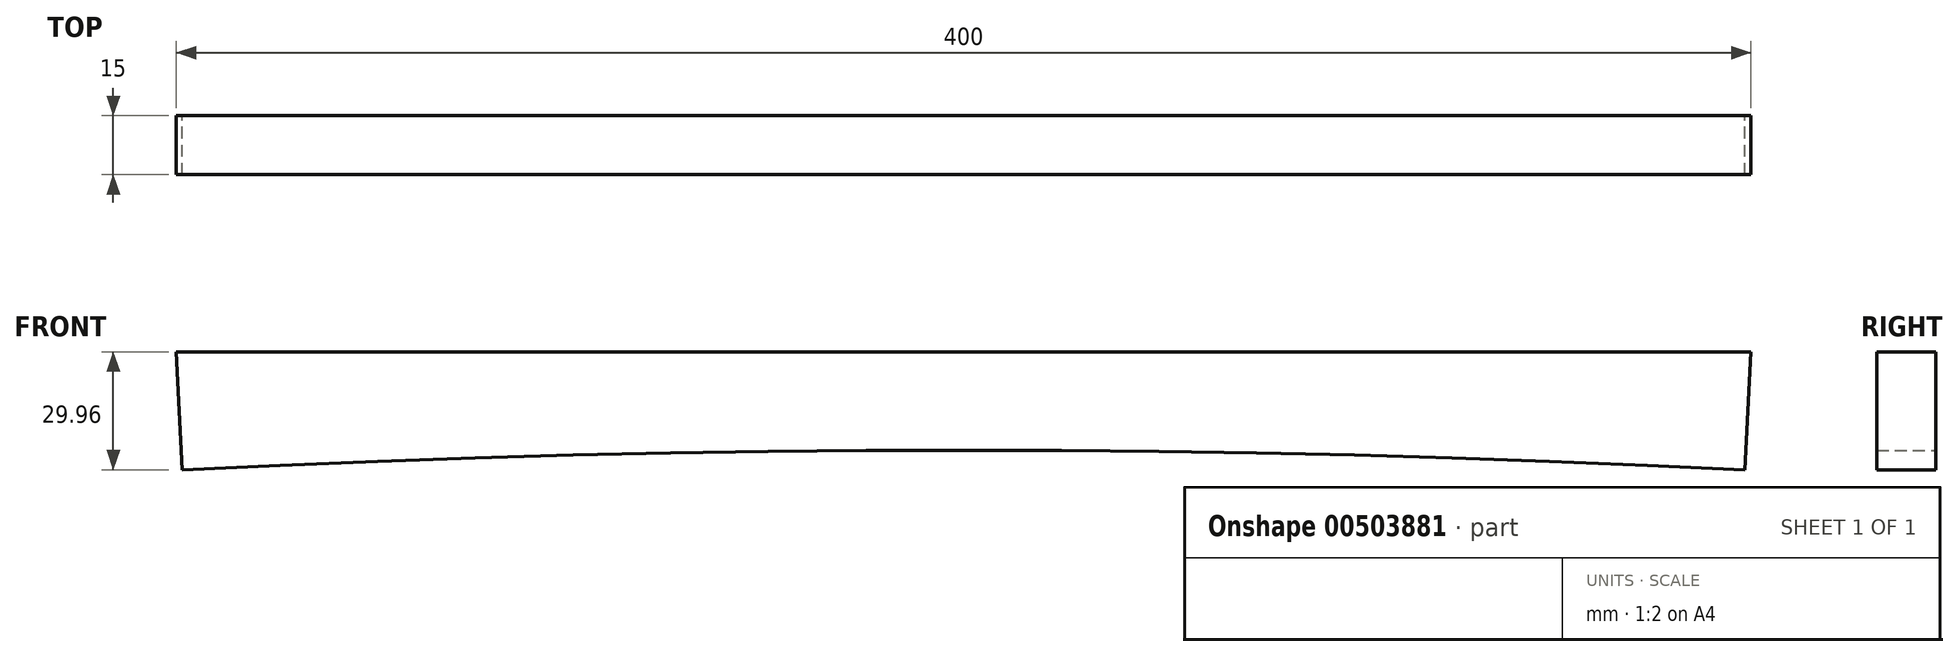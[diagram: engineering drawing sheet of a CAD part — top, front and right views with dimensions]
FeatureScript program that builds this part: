
annotation { "Feature Type Name" : "Feature", "Feature Type Description" : "" }
export const myFeature = defineFeature(function(context is Context, id is Id, definition is map)
    precondition{}
    {
        {
            var Q0;
            Q0=qCreatedBy(makeId("Front.planeOp"),FACE);
            var sketch = newSketch(context, id + "F0", { "sketchPlane" : qUnion([Q0])});
            skLineSegment(sketch, "E0", {"start": v(-200, 0) * mm, "end": v(200, 0) * mm});
            skPoint(sketch, "E1", {"position": v(0, 0) * mm});
            skLineSegment(sketch, "E2", {"start": v(0, 0) * mm, "end": v(0, -4000) * mm});
            skLineSegment(sketch, "E3", {"start": v(-198.5, -29.96) * mm, "end": v(-200, 0) * mm});
            skLineSegment(sketch, "E4", {"start": v(198.5, -29.96) * mm, "end": v(200, 0) * mm});
            skPoint(sketch, "E5", {"position": v(-198.5, -29.96) * mm});
            skPoint(sketch, "E6", {"position": v(198.5, -29.96) * mm});
            skArc(sketch, "E7", {"start": v(-198.5, -29.96) * mm, "mid": v(0, -25) * mm, "end": v(198.5, -29.96) * mm});
            skPoint(sketch, "E8", {"position": v(-198.6, -27.97) * mm});
            skArc(sketch, "E9", {"start": v(-198.6, -27.97) * mm, "mid": v(0, -23) * mm, "end": v(198.6, -27.97) * mm});
            skLineSegment(sketch, "E10", {"start": v(-199.9, -2) * mm, "end": v(199.9, -2) * mm});
            skSolve(sketch);
        }
        {
            var Q0;
            {var subQ0=sQuery(id+"F0.wireOp",EDGE,"E3");var subQ1=sQuery(id+"F0.wireOp",EDGE,"E0");var subQ2=makeQuery(id+"F0.imprint","INTERSECT",VERTEX,{"derivedFrom":[subQ1,subQ0]});Q0=makeQuery(id+"F0.imprint","IMPRINT",FACE,{"disambiguationData":[TD([[makeQuery(id+"F0.imprint","IMPRINT",EDGE,{"disambiguationData":[TD([[subQ2,-1.0]])],"derivedFrom":subQ1}),-1.0]])]});}
            var Q1;
            {var subQ0=sQuery(id+"F0.wireOp",EDGE,"E7");var subQ1=sQuery(id+"F0.wireOp",EDGE,"E2");var subQ2=makeQuery(id+"F0.imprint","INTERSECT",VERTEX,{"derivedFrom":[subQ1,subQ0]});Q1=makeQuery(id+"F0.imprint","IMPRINT",FACE,{"disambiguationData":[TD([[makeQuery(id+"F0.imprint","IMPRINT",EDGE,{"disambiguationData":[TD([[subQ2,1.0]])],"derivedFrom":subQ1}),1.0]])]});}
            var Q2;
            {var subQ0=sQuery(id+"F0.wireOp",EDGE,"E10");var subQ1=sQuery(id+"F0.wireOp",EDGE,"E2");var subQ2=makeQuery(id+"F0.imprint","INTERSECT",VERTEX,{"derivedFrom":[subQ1,subQ0]});Q2=makeQuery(id+"F0.imprint","IMPRINT",FACE,{"disambiguationData":[TD([[makeQuery(id+"F0.imprint","IMPRINT",EDGE,{"disambiguationData":[TD([[subQ2,-1.0]])],"derivedFrom":subQ1}),1.0]])]});}
            var Q3;
            {var subQ0=sQuery(id+"F0.wireOp",EDGE,"E10");var subQ1=sQuery(id+"F0.wireOp",EDGE,"E2");var subQ2=makeQuery(id+"F0.imprint","INTERSECT",VERTEX,{"derivedFrom":[subQ1,subQ0]});Q3=makeQuery(id+"F0.imprint","IMPRINT",FACE,{"disambiguationData":[TD([[makeQuery(id+"F0.imprint","IMPRINT",EDGE,{"disambiguationData":[TD([[subQ2,-1.0]])],"derivedFrom":subQ1}),-1.0]])]});}
            var Q4;
            {var subQ0=sQuery(id+"F0.wireOp",EDGE,"E4");var subQ1=sQuery(id+"F0.wireOp",EDGE,"E0");var subQ2=makeQuery(id+"F0.imprint","INTERSECT",VERTEX,{"derivedFrom":[subQ1,subQ0]});Q4=makeQuery(id+"F0.imprint","IMPRINT",FACE,{"disambiguationData":[TD([[makeQuery(id+"F0.imprint","IMPRINT",EDGE,{"disambiguationData":[TD([[subQ2,1.0]])],"derivedFrom":subQ1}),-1.0]])]});}
            var Q5;
            {var subQ0=sQuery(id+"F0.wireOp",EDGE,"E7");var subQ1=sQuery(id+"F0.wireOp",EDGE,"E2");var subQ2=makeQuery(id+"F0.imprint","INTERSECT",VERTEX,{"derivedFrom":[subQ1,subQ0]});Q5=makeQuery(id+"F0.imprint","IMPRINT",FACE,{"disambiguationData":[TD([[makeQuery(id+"F0.imprint","IMPRINT",EDGE,{"disambiguationData":[TD([[subQ2,1.0]])],"derivedFrom":subQ1}),-1.0]])]});}
            extrude(context, id + "F1", {"entities" : qUnion([Q0, Q1, Q2, Q3, Q4, Q5]), "depth" : 15 * mm});
        }
    });
